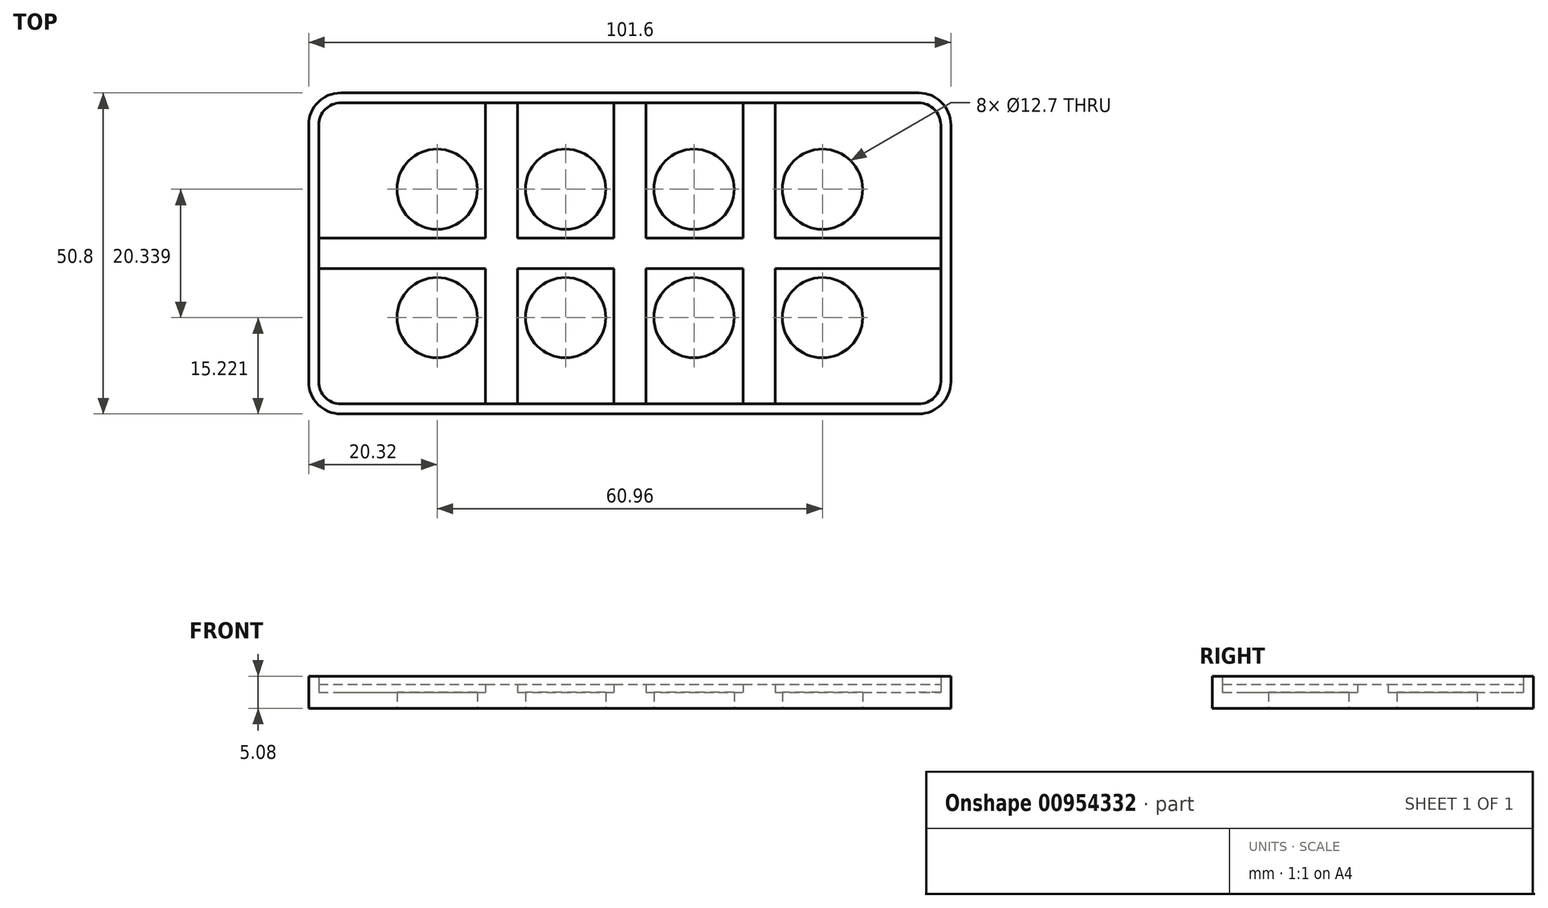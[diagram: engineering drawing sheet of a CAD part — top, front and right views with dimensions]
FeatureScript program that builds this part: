
annotation { "Feature Type Name" : "Feature", "Feature Type Description" : "" }
export const myFeature = defineFeature(function(context is Context, id is Id, definition is map)
    precondition{}
    {
        {
            var Q0;
            Q0=qCreatedBy(makeId("Top.planeOp"),FACE);
            var sketch = newSketch(context, id + "F0", { "sketchPlane" : qUnion([Q0])});
            skLineSegment(sketch, "E0.bottom", {"start": v(-45.72, -25.4) * mm, "end": v(45.72, -25.4) * mm});
            skLineSegment(sketch, "E0.top", {"start": v(-45.72, 25.4) * mm, "end": v(45.72, 25.4) * mm});
            skLineSegment(sketch, "E0.left", {"start": v(-50.8, -20.32) * mm, "end": v(-50.8, 20.32) * mm});
            skLineSegment(sketch, "E0.right", {"start": v(50.8, -20.32) * mm, "end": v(50.8, 20.32) * mm});
            skPoint(sketch, "E0.middle", {"position": v(0, 0) * mm});
            skPoint(sketch, "E1.visualSharp", {"position": v(-50.8, 25.4) * mm});
            skArc(sketch, "E1.filletArc", {"start": v(-45.72, 25.4) * mm, "mid": v(-49.31, 23.91) * mm, "end": v(-50.8, 20.32) * mm});
            skPoint(sketch, "E2.visualSharp", {"position": v(-50.8, -25.4) * mm});
            skArc(sketch, "E2.filletArc", {"start": v(-50.8, -20.32) * mm, "mid": v(-49.31, -23.91) * mm, "end": v(-45.72, -25.4) * mm});
            skPoint(sketch, "E3.visualSharp", {"position": v(50.8, 25.4) * mm});
            skArc(sketch, "E3.filletArc", {"start": v(50.8, 20.32) * mm, "mid": v(49.31, 23.91) * mm, "end": v(45.72, 25.4) * mm});
            skPoint(sketch, "E4.visualSharp", {"position": v(50.8, -25.4) * mm});
            skArc(sketch, "E4.filletArc", {"start": v(45.72, -25.4) * mm, "mid": v(49.31, -23.91) * mm, "end": v(50.8, -20.32) * mm});
            skCircle(sketch, "E5", {"center": v(-30.48, 10.16) * mm, "radius": 6.35 * mm});
            skCircle(sketch, "E6", {"center": v(-30.48, -10.16) * mm, "radius": 6.35 * mm});
            skCircle(sketch, "E7", {"center": v(-10.16, 10.16) * mm, "radius": 6.35 * mm});
            skCircle(sketch, "E8", {"center": v(-10.16, -10.16) * mm, "radius": 6.35 * mm});
            skCircle(sketch, "E9", {"center": v(10.16, 10.16) * mm, "radius": 6.35 * mm});
            skCircle(sketch, "E10", {"center": v(10.16, -10.16) * mm, "radius": 6.35 * mm});
            skCircle(sketch, "E11", {"center": v(30.48, 10.16) * mm, "radius": 6.35 * mm});
            skCircle(sketch, "E12", {"center": v(30.48, -10.18) * mm, "radius": 6.35 * mm});
            skArc(sketch, "E13.0", {"start": v(-45.72, 23.81) * mm, "mid": v(-48.19, 22.79) * mm, "end": v(-49.21, 20.32) * mm});
            skLineSegment(sketch, "E13.1", {"start": v(-49.21, -20.32) * mm, "end": v(-49.21, 20.32) * mm});
            skLineSegment(sketch, "E13.2", {"start": v(-45.72, 23.81) * mm, "end": v(45.72, 23.81) * mm});
            skArc(sketch, "E13.3", {"start": v(-49.21, -20.32) * mm, "mid": v(-48.19, -22.79) * mm, "end": v(-45.72, -23.81) * mm});
            skArc(sketch, "E13.4", {"start": v(49.21, 20.32) * mm, "mid": v(48.19, 22.79) * mm, "end": v(45.72, 23.81) * mm});
            skLineSegment(sketch, "E13.5", {"start": v(49.21, -20.32) * mm, "end": v(49.21, 20.32) * mm});
            skArc(sketch, "E13.6", {"start": v(45.72, -23.81) * mm, "mid": v(48.19, -22.79) * mm, "end": v(49.21, -20.32) * mm});
            skLineSegment(sketch, "E13.7", {"start": v(-45.72, -23.81) * mm, "end": v(45.72, -23.81) * mm});
            skLineSegment(sketch, "E14.bottom", {"start": v(-2.54, -23.81) * mm, "end": v(2.54, -23.81) * mm});
            skLineSegment(sketch, "E14.top", {"start": v(-2.54, 23.81) * mm, "end": v(2.54, 23.81) * mm});
            skLineSegment(sketch, "E14.left", {"start": v(-2.54, -23.81) * mm, "end": v(-2.54, 23.81) * mm});
            skLineSegment(sketch, "E14.right", {"start": v(2.54, -23.81) * mm, "end": v(2.54, 23.81) * mm});
            skLineSegment(sketch, "E15.bottom", {"start": v(-49.21, -2.43) * mm, "end": v(49.21, -2.43) * mm});
            skLineSegment(sketch, "E15.top", {"start": v(-49.21, 2.43) * mm, "end": v(49.21, 2.43) * mm});
            skLineSegment(sketch, "E15.left", {"start": v(-49.21, -2.43) * mm, "end": v(-49.21, 2.43) * mm});
            skLineSegment(sketch, "E15.right", {"start": v(49.21, -2.43) * mm, "end": v(49.21, 2.43) * mm});
            skLineSegment(sketch, "E16.left", {"start": v(-22.8, -23.81) * mm, "end": v(-22.8, 23.81) * mm});
            skLineSegment(sketch, "E16.right", {"start": v(-17.73, -23.81) * mm, "end": v(-17.73, 23.81) * mm});
            skLineSegment(sketch, "E17.left", {"start": v(17.92, -23.81) * mm, "end": v(17.92, 23.81) * mm});
            skLineSegment(sketch, "E17.right", {"start": v(23, -23.81) * mm, "end": v(23, 23.81) * mm});
            skSolve(sketch);
        }
        {
            var Q0;
            Q0=makeQuery(id+"F0.imprint","IMPRINT",FACE,{"disambiguationData":[TD([[makeQuery(id+"F0.imprint","IMPRINT",EDGE,{"derivedFrom":sQuery(id+"F0.wireOp",EDGE,"E0.bottom")}),1.0]])]});
            extrude(context, id + "F1", {"entities" : qUnion([Q0]), "depth" : 5.08 * mm, "offsetDistance" : 25.4 * mm});
        }
        {
            var Q0;
            {var subQ0=sQuery(id+"F0.wireOp",EDGE,"E16.right");var subQ1=sQuery(id+"F0.wireOp",EDGE,"E13.2");var subQ2=makeQuery(id+"F0.imprint","INTERSECT",VERTEX,{"derivedFrom":[subQ1,subQ0]});Q0=makeQuery(id+"F0.imprint","IMPRINT",FACE,{"disambiguationData":[TD([[makeQuery(id+"F0.imprint","IMPRINT",EDGE,{"disambiguationData":[TD([[subQ2,1.0]])],"derivedFrom":subQ1}),-1.0]])]});}
            var Q1;
            {var subQ0=sQuery(id+"F0.wireOp",EDGE,"E16.left");var subQ1=sQuery(id+"F0.wireOp",EDGE,"E15.bottom");var subQ2=makeQuery(id+"F0.imprint","INTERSECT",VERTEX,{"derivedFrom":[subQ1,subQ0]});Q1=makeQuery(id+"F0.imprint","IMPRINT",FACE,{"disambiguationData":[TD([[makeQuery(id+"F0.imprint","IMPRINT",EDGE,{"disambiguationData":[TD([[subQ2,-1.0]])],"derivedFrom":subQ1}),1.0]])]});}
            var Q2;
            {var subQ0=sQuery(id+"F0.wireOp",EDGE,"E15.top");var subQ1=sQuery(id+"F0.wireOp",EDGE,"E13.1");var subQ2=makeQuery(id+"F0.imprint","INTERSECT",VERTEX,{"derivedFrom":[subQ1,subQ0]});Q2=makeQuery(id+"F0.imprint","IMPRINT",FACE,{"disambiguationData":[TD([[makeQuery(id+"F0.imprint","IMPRINT",EDGE,{"disambiguationData":[TD([[subQ2,1.0]])],"derivedFrom":subQ1}),-1.0]])]});}
            var Q3;
            {var subQ0=sQuery(id+"F0.wireOp",EDGE,"E16.left");var subQ1=sQuery(id+"F0.wireOp",EDGE,"E13.7");var subQ2=makeQuery(id+"F0.imprint","INTERSECT",VERTEX,{"derivedFrom":[subQ1,subQ0]});Q3=makeQuery(id+"F0.imprint","IMPRINT",FACE,{"disambiguationData":[TD([[makeQuery(id+"F0.imprint","IMPRINT",EDGE,{"disambiguationData":[TD([[subQ2,-1.0]])],"derivedFrom":subQ1}),1.0]])]});}
            var Q4;
            {var subQ0=sQuery(id+"F0.wireOp",EDGE,"E15.top");var subQ1=sQuery(id+"F0.wireOp",EDGE,"E14.left");var subQ2=makeQuery(id+"F0.imprint","INTERSECT",VERTEX,{"derivedFrom":[subQ1,subQ0]});Q4=makeQuery(id+"F0.imprint","IMPRINT",FACE,{"disambiguationData":[TD([[makeQuery(id+"F0.imprint","IMPRINT",EDGE,{"disambiguationData":[TD([[subQ2,1.0]])],"derivedFrom":subQ1}),1.0]])]});}
            var Q5;
            {var subQ0=sQuery(id+"F0.wireOp",EDGE,"E14.right");var subQ1=sQuery(id+"F0.wireOp",EDGE,"E13.2");var subQ2=makeQuery(id+"F0.imprint","INTERSECT",VERTEX,{"derivedFrom":[subQ1,subQ0]});Q5=makeQuery(id+"F0.imprint","IMPRINT",FACE,{"disambiguationData":[TD([[makeQuery(id+"F0.imprint","IMPRINT",EDGE,{"disambiguationData":[TD([[subQ2,1.0]])],"derivedFrom":subQ1}),-1.0]])]});}
            var Q6;
            {var subQ0=sQuery(id+"F0.wireOp",EDGE,"E14.left");var subQ1=sQuery(id+"F0.wireOp",EDGE,"E13.7");var subQ2=makeQuery(id+"F0.imprint","INTERSECT",VERTEX,{"derivedFrom":[subQ1,subQ0]});Q6=makeQuery(id+"F0.imprint","IMPRINT",FACE,{"disambiguationData":[TD([[makeQuery(id+"F0.imprint","IMPRINT",EDGE,{"disambiguationData":[TD([[subQ2,-1.0]])],"derivedFrom":subQ1}),1.0]])]});}
            var Q7;
            {var subQ0=sQuery(id+"F0.wireOp",EDGE,"E15.top");var subQ1=sQuery(id+"F0.wireOp",EDGE,"E14.left");var subQ2=makeQuery(id+"F0.imprint","INTERSECT",VERTEX,{"derivedFrom":[subQ1,subQ0]});Q7=makeQuery(id+"F0.imprint","IMPRINT",FACE,{"disambiguationData":[TD([[makeQuery(id+"F0.imprint","IMPRINT",EDGE,{"disambiguationData":[TD([[subQ2,1.0]])],"derivedFrom":subQ1}),-1.0]])]});}
            var Q8;
            {var subQ0=sQuery(id+"F0.wireOp",EDGE,"E15.top");var subQ1=sQuery(id+"F0.wireOp",EDGE,"E14.right");var subQ2=makeQuery(id+"F0.imprint","INTERSECT",VERTEX,{"derivedFrom":[subQ1,subQ0]});Q8=makeQuery(id+"F0.imprint","IMPRINT",FACE,{"disambiguationData":[TD([[makeQuery(id+"F0.imprint","IMPRINT",EDGE,{"disambiguationData":[TD([[subQ2,1.0]])],"derivedFrom":subQ1}),-1.0]])]});}
            var Q9;
            {var subQ0=sQuery(id+"F0.wireOp",EDGE,"E17.right");var subQ1=sQuery(id+"F0.wireOp",EDGE,"E15.bottom");var subQ2=makeQuery(id+"F0.imprint","INTERSECT",VERTEX,{"derivedFrom":[subQ1,subQ0]});Q9=makeQuery(id+"F0.imprint","IMPRINT",FACE,{"disambiguationData":[TD([[makeQuery(id+"F0.imprint","IMPRINT",EDGE,{"disambiguationData":[TD([[subQ2,1.0]])],"derivedFrom":subQ1}),1.0]])]});}
            var Q10;
            {var subQ0=sQuery(id+"F0.wireOp",EDGE,"E17.right");var subQ1=sQuery(id+"F0.wireOp",EDGE,"E13.2");var subQ2=makeQuery(id+"F0.imprint","INTERSECT",VERTEX,{"derivedFrom":[subQ1,subQ0]});Q10=makeQuery(id+"F0.imprint","IMPRINT",FACE,{"disambiguationData":[TD([[makeQuery(id+"F0.imprint","IMPRINT",EDGE,{"disambiguationData":[TD([[subQ2,1.0]])],"derivedFrom":subQ1}),-1.0]])]});}
            var Q11;
            {var subQ0=sQuery(id+"F0.wireOp",EDGE,"E17.right");var subQ1=sQuery(id+"F0.wireOp",EDGE,"E13.7");var subQ2=makeQuery(id+"F0.imprint","INTERSECT",VERTEX,{"derivedFrom":[subQ1,subQ0]});Q11=makeQuery(id+"F0.imprint","IMPRINT",FACE,{"disambiguationData":[TD([[makeQuery(id+"F0.imprint","IMPRINT",EDGE,{"disambiguationData":[TD([[subQ2,1.0]])],"derivedFrom":subQ1}),1.0]])]});}
            var Q12;
            {var subQ0=sQuery(id+"F0.wireOp",EDGE,"E15.top");var subQ1=sQuery(id+"F0.wireOp",EDGE,"E13.5");var subQ2=makeQuery(id+"F0.imprint","INTERSECT",VERTEX,{"derivedFrom":[subQ1,subQ0]});Q12=makeQuery(id+"F0.imprint","IMPRINT",FACE,{"disambiguationData":[TD([[makeQuery(id+"F0.imprint","IMPRINT",EDGE,{"disambiguationData":[TD([[subQ2,1.0]])],"derivedFrom":subQ1}),1.0]])]});}
            extrude(context, id + "F2", {"entities" : qUnion([Q0, Q1, Q2, Q3, Q4, Q5, Q6, Q7, Q8, Q9, Q10, Q11, Q12]), "operationType" : NewBodyOperationType.ADD, "depth" : 3.8 * mm, "offsetDistance" : 25.4 * mm});
        }
        {
            var Q0;
            Q0=makeQuery(id+"F0.imprint","IMPRINT",FACE,{"disambiguationData":[TD([[makeQuery(id+"F0.imprint","IMPRINT",EDGE,{"derivedFrom":sQuery(id+"F0.wireOp",EDGE,"E5")}),-1.0]])]});
            var Q1;
            Q1=makeQuery(id+"F0.imprint","IMPRINT",FACE,{"disambiguationData":[TD([[makeQuery(id+"F0.imprint","IMPRINT",EDGE,{"derivedFrom":sQuery(id+"F0.wireOp",EDGE,"E7")}),-1.0]])]});
            var Q2;
            Q2=makeQuery(id+"F0.imprint","IMPRINT",FACE,{"disambiguationData":[TD([[makeQuery(id+"F0.imprint","IMPRINT",EDGE,{"derivedFrom":sQuery(id+"F0.wireOp",EDGE,"E9")}),-1.0]])]});
            var Q3;
            Q3=makeQuery(id+"F0.imprint","IMPRINT",FACE,{"disambiguationData":[TD([[makeQuery(id+"F0.imprint","IMPRINT",EDGE,{"derivedFrom":sQuery(id+"F0.wireOp",EDGE,"E11")}),-1.0]])]});
            var Q4;
            Q4=makeQuery(id+"F0.imprint","IMPRINT",FACE,{"disambiguationData":[TD([[makeQuery(id+"F0.imprint","IMPRINT",EDGE,{"derivedFrom":sQuery(id+"F0.wireOp",EDGE,"E12")}),-1.0]])]});
            var Q5;
            Q5=makeQuery(id+"F0.imprint","IMPRINT",FACE,{"disambiguationData":[TD([[makeQuery(id+"F0.imprint","IMPRINT",EDGE,{"derivedFrom":sQuery(id+"F0.wireOp",EDGE,"E10")}),-1.0]])]});
            var Q6;
            Q6=makeQuery(id+"F0.imprint","IMPRINT",FACE,{"disambiguationData":[TD([[makeQuery(id+"F0.imprint","IMPRINT",EDGE,{"derivedFrom":sQuery(id+"F0.wireOp",EDGE,"E8")}),-1.0]])]});
            var Q7;
            Q7=makeQuery(id+"F0.imprint","IMPRINT",FACE,{"disambiguationData":[TD([[makeQuery(id+"F0.imprint","IMPRINT",EDGE,{"derivedFrom":sQuery(id+"F0.wireOp",EDGE,"E6")}),-1.0]])]});
            extrude(context, id + "F3", {"entities" : qUnion([Q0, Q1, Q2, Q3, Q4, Q5, Q6, Q7]), "operationType" : NewBodyOperationType.ADD, "depth" : 2.54 * mm, "offsetDistance" : 25.4 * mm});
        }
    });
